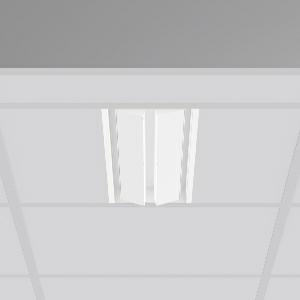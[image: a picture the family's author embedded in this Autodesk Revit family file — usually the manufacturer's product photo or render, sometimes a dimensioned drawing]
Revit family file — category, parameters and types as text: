
# Revit family: tx-move_901739_002_76_f09a
name_source: partatom
category: Lighting Fixtures
units: mm (PartAtom-declared; Revit-internal decimal feet)

## family parameters
Cut with Voids When Loaded = No
Host = Face
Light Source = No
Part Type = Normal
Room Calculation Point = No
Round Connector Dimension = Use Diameter
Shared = No

## types (1)
- MultiLumen 1 (1 x LED Modul 830, 2425 lm, 3000)
    Apparent Load = 35 VA
    Approval mark = CE
    CIE Flux Codes = 47 79 96 100 100
    Color Rendering = 80
    Color Temperature = 3000
    Default Elevation = 1800 mm
    Description = Series: TX-MOVE
Einlege/Einbau-Flächenstrahler. Housing: sheet steel, powder-coated. 2xSwivel range: 90°. High-efficiency LED units with flush-mounted opal diffuser made of non-yellowing PMMA. Symmetrical wide beam light emission. Suitable for laying in grid ceiling module 625. Connected converter included in separate gearbox.Suitable for through-wiring.MultiLumen: Luminous flux adjustable in 3 steps. Accessories: Mounting frame for installation in suspended ceilings. Environmentally friendly and resource-saving due to replaceable and recyclable components. 
Colour: traffic white, matt (RAL 9016)
Length: 622 mm
Width: 190 mm
Height: 39 mm
Cut-out length: 602 mm
Cut-out width: 174 mm
Recess height: 100 mm
Lamp: LED
Socket: without socket
Colour temperature: 3000K
Colour rendering index (CRI): 80
System power: 35 W
Rated luminous flux: 4850 lm
Luminous efficiency: 139 lm/W
System power 2: 47 W
Rated luminous flux 2: 6250 lm
Luminous efficiency 2: 133 lm/W
System power 3: 68 W
Rated luminous flux 3: 8450 lm
Luminous efficiency 3: 124 lm/W
Control gear: Dimmable EVG, DALI
Protection class: I
Type of protection: IP 20
    Height = 0 mm  [stored 0 ft]
    Lamp = 1 x LED Modul 830
    Lamp Light Flux = 2425 lm
    Lamp count = 1
    Length = 622 mm
    Lifetime = 50000 h
    Luminous efficacy = 139 lm/W
    Manufacturer = RZB
    ModVariant = No
    Model = 901739.002.76
    Mounting Place = Ceiling, Wall
    Mounting Type = Recessed
    Number of Poles = 1
    OnlyDefault = Yes
    Power Factor = 1
    Product Name = TX-MOVE
    Product group = Recessed projectors
    ProductGroupID = 401
    Protection Class = Protection class I
    Protection Degree = IP 20
    RLX_Detail_Level = 1
    RLX_Emergency_Light_Flux = 0 lm
    RLX_Emergency_Type = 0
    RLX_Emergency_Type_DB = No
    RlxData = <blob elided: 28969 chars, md5=7ac760e3>
    Socket = socket
    Standby Power = 0 W
    System Light Flux = 4850 lm
    System Power = 35 W
    Type Comments = MultiLumen 1
    Type Image = 901739.002.jpg
    URL = http://relux.com
    VarID = multilumen_1
    Voltage = 230 V
    Voltage Range = 220-240 V
    Weight = 0.00 kg
    Width = 190 mm  [stored 0.62336 ft]

note: [stored X ft] marks values corroborated as IEEE doubles in the binary element streams (Revit-internal decimal feet)

## geometry (parser evidence)
native form markers: Blend x4, Sweep x15
no freeform markers — native parametric forms only
